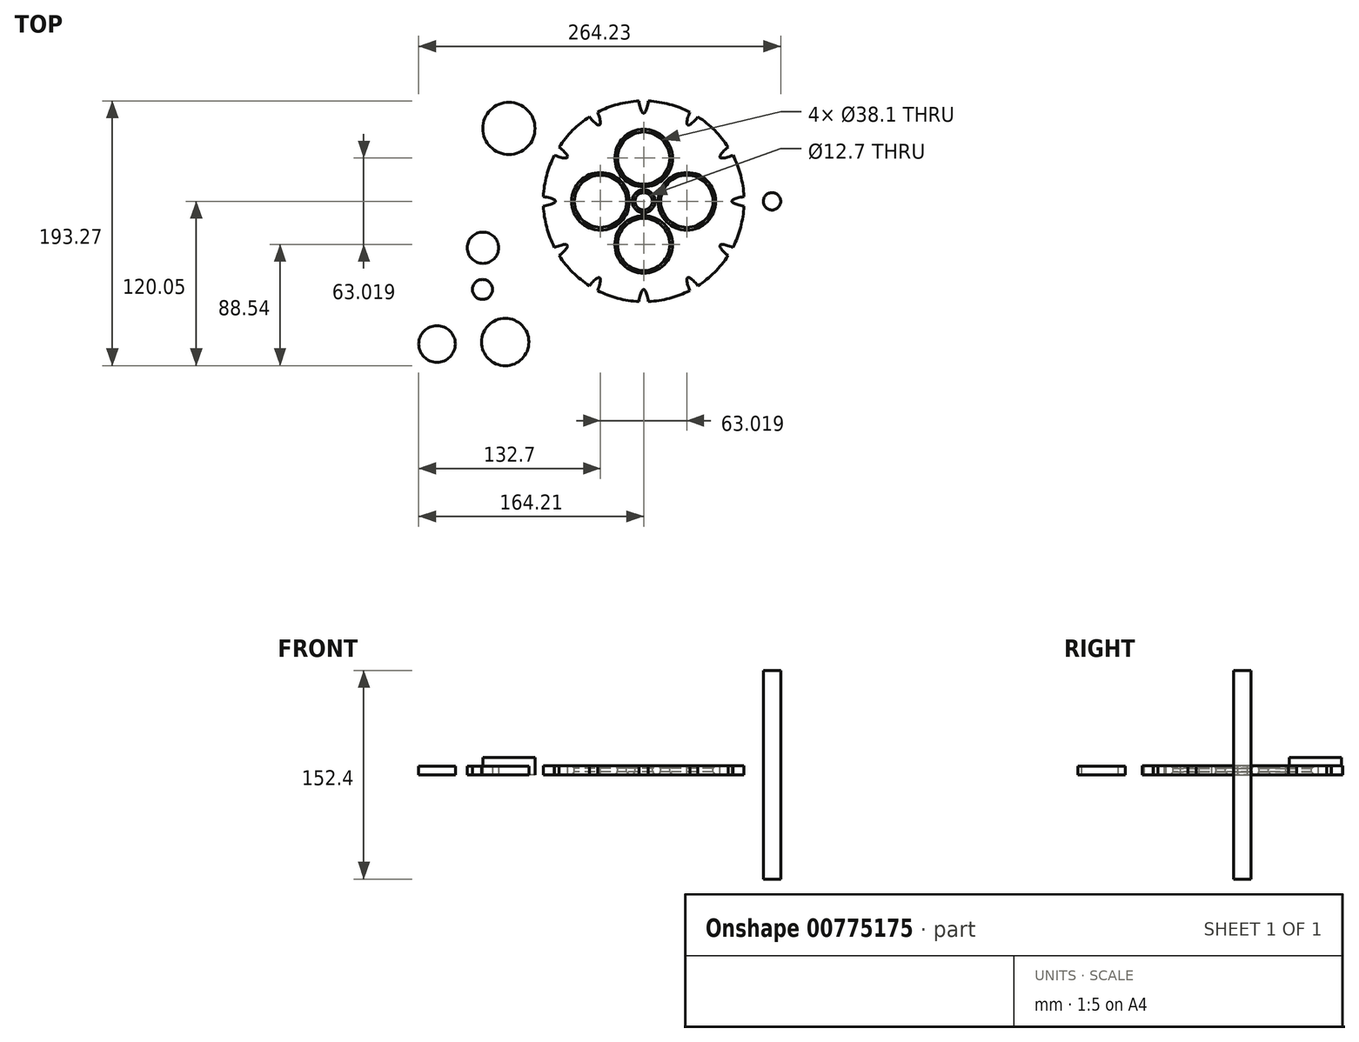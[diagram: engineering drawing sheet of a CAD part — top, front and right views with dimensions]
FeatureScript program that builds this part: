
annotation { "Feature Type Name" : "Feature", "Feature Type Description" : "" }
export const myFeature = defineFeature(function(context is Context, id is Id, definition is map)
    precondition{}
    {
        {
            var Q0;
            Q0=qCreatedBy(makeId("Top.planeOp"),FACE);
            var sketch = newSketch(context, id + "F0", { "sketchPlane" : qUnion([Q0])});
            skCircle(sketch, "E0", {"center": v(0, 0) * mm, "radius": 73.3 * mm});
            skSolve(sketch);
        }
        {
            var Q0;
            Q0=makeQuery(id+"F0.imprint","IMPRINT",FACE,{"disambiguationData":[TD([[makeQuery(id+"F0.imprint","IMPRINT",EDGE,{"derivedFrom":sQuery(id+"F0.wireOp",EDGE,"E0")}),1.0]])]});
            extrude(context, id + "F1", {"entities" : qUnion([Q0]), "depth" : 6.6 * mm, "offsetDistance" : 25.4 * mm});
        }
        {
            var Q0;
            Q0=qCreatedBy(makeId("Top.planeOp"),FACE);
            var sketch = newSketch(context, id + "F2", { "sketchPlane" : qUnion([Q0])});
            skEllipse(sketch, "E1", {"center": v(0, 87.88) * mm, "majorRadius": 23.55 * mm, "minorRadius": 4.4 * mm, "majorAxis": v(0, -1)});
            skEllipse(sketch, "E2.1.0", {"center": v(-43.94, 76.1) * mm, "majorRadius": 23.55 * mm, "minorRadius": 4.4 * mm, "majorAxis": v(0.5, -0.87)});
            skEllipse(sketch, "E2.2.0", {"center": v(-76.1, 43.94) * mm, "majorRadius": 23.55 * mm, "minorRadius": 4.4 * mm, "majorAxis": v(0.87, -0.5)});
            skEllipse(sketch, "E2.3.0", {"center": v(-87.88, 0) * mm, "majorRadius": 23.55 * mm, "minorRadius": 4.4 * mm, "majorAxis": v(1, 0)});
            skEllipse(sketch, "E2.4.0", {"center": v(-76.1, -43.94) * mm, "majorRadius": 23.55 * mm, "minorRadius": 4.4 * mm, "majorAxis": v(0.87, 0.5)});
            skEllipse(sketch, "E2.5.0", {"center": v(-43.94, -76.1) * mm, "majorRadius": 23.55 * mm, "minorRadius": 4.4 * mm, "majorAxis": v(0.5, 0.87)});
            skEllipse(sketch, "E2.6.0", {"center": v(0, -87.88) * mm, "majorRadius": 23.55 * mm, "minorRadius": 4.4 * mm, "majorAxis": v(0, 1)});
            skEllipse(sketch, "E2.7.0", {"center": v(43.94, -76.1) * mm, "majorRadius": 23.55 * mm, "minorRadius": 4.4 * mm, "majorAxis": v(-0.5, 0.87)});
            skEllipse(sketch, "E2.8.0", {"center": v(76.1, -43.94) * mm, "majorRadius": 23.55 * mm, "minorRadius": 4.4 * mm, "majorAxis": v(-0.87, 0.5)});
            skEllipse(sketch, "E2.9.0", {"center": v(87.88, 0) * mm, "majorRadius": 23.55 * mm, "minorRadius": 4.4 * mm, "majorAxis": v(-1, 0)});
            skEllipse(sketch, "E2.10.0", {"center": v(76.1, 43.94) * mm, "majorRadius": 23.55 * mm, "minorRadius": 4.4 * mm, "majorAxis": v(-0.87, -0.5)});
            skEllipse(sketch, "E2.11.0", {"center": v(43.94, 76.1) * mm, "majorRadius": 23.55 * mm, "minorRadius": 4.4 * mm, "majorAxis": v(-0.5, -0.87)});
            skPoint(sketch, "E2.center", {"position": v(0, 0) * mm});
            skSolve(sketch);
        }
        {
            var Q0;
            Q0=makeQuery(id+"F2.imprint","IMPRINT",FACE,{"disambiguationData":[TD([[makeQuery(id+"F2.imprint","IMPRINT",EDGE,{"derivedFrom":sQuery(id+"F2.wireOp",EDGE,"E1")}),1.0]])]});
            extrude(context, id + "F3", {"entities" : qUnion([Q0]), "operationType" : NewBodyOperationType.REMOVE, "depth" : 25.4 * mm, "offsetDistance" : 25.4 * mm, "hasSecondDirection" : true, "secondDirectionOppositeDirection" : true, "secondDirectionDepth" : 25.4 * mm});
        }
        {
            var Q0;
            Q0 = qSketchRegion(id + "F2", true);
            extrude(context, id + "F4", {"entities" : qUnion([Q0]), "operationType" : NewBodyOperationType.REMOVE, "depth" : 25.4 * mm, "offsetDistance" : 25.4 * mm, "hasSecondDirection" : true, "secondDirectionOppositeDirection" : true, "secondDirectionDepth" : 25.4 * mm});
        }
        {
            var Q0;
            Q0=makeQuery(id+"F1.opExtrude","CAP_FACE",FACE,{"disambiguationData":[OSD([sQuery(id+"F0.wireOp",EDGE,"E0")])],"isStart":false});
            var sketch = newSketch(context, id + "F5", { "sketchPlane" : qUnion([Q0])});
            skCircle(sketch, "E3", {"center": v(0, 31.5) * mm, "radius": 19.05 * mm});
            skCircle(sketch, "E4.1.0", {"center": v(-31.5, 0) * mm, "radius": 19.05 * mm});
            skCircle(sketch, "E4.2.0", {"center": v(0, -31.5) * mm, "radius": 19.05 * mm});
            skCircle(sketch, "E4.3.0", {"center": v(31.5, 0) * mm, "radius": 19.05 * mm});
            skPoint(sketch, "E4.center", {"position": v(0, 0) * mm});
            skSolve(sketch);
        }
        {
            var Q0;
            Q0=makeQuery(id+"F5.imprint","IMPRINT",FACE,{"disambiguationData":[TD([[makeQuery(id+"F5.imprint","IMPRINT",EDGE,{"derivedFrom":sQuery(id+"F5.wireOp",EDGE,"E3")}),1.0]])]});
            var Q1;
            Q1=makeQuery(id+"F5.imprint","IMPRINT",FACE,{"disambiguationData":[TD([[makeQuery(id+"F5.imprint","IMPRINT",EDGE,{"derivedFrom":sQuery(id+"F5.wireOp",EDGE,"E4.1.0")}),1.0]])]});
            var Q2;
            Q2=makeQuery(id+"F5.imprint","IMPRINT",FACE,{"disambiguationData":[TD([[makeQuery(id+"F5.imprint","IMPRINT",EDGE,{"derivedFrom":sQuery(id+"F5.wireOp",EDGE,"E4.3.0")}),1.0]])]});
            var Q3;
            Q3=makeQuery(id+"F5.imprint","IMPRINT",FACE,{"disambiguationData":[TD([[makeQuery(id+"F5.imprint","IMPRINT",EDGE,{"derivedFrom":sQuery(id+"F5.wireOp",EDGE,"E4.2.0")}),1.0]])]});
            extrude(context, id + "F6", {"entities" : qUnion([Q0, Q1, Q2, Q3]), "operationType" : NewBodyOperationType.REMOVE, "oppositeDirection" : true, "depth" : 25.4 * mm, "offsetDistance" : 25.4 * mm, "hasSecondDirection" : true, "secondDirectionOppositeDirection" : false, "secondDirectionDepth" : 25.4 * mm});
        }
        {
            var Q0;
            Q0=makeQuery(id+"F1.opExtrude","CAP_FACE",FACE,{"disambiguationData":[OSD([sQuery(id+"F0.wireOp",EDGE,"E0")])],"isStart":false});
            var sketch = newSketch(context, id + "F7", { "sketchPlane" : qUnion([Q0])});
            skCircle(sketch, "E5", {"center": v(0, 0) * mm, "radius": 6.35 * mm});
            skSolve(sketch);
        }
        {
            var Q0;
            Q0=makeQuery(id+"F7.imprint","IMPRINT",FACE,{"disambiguationData":[TD([[makeQuery(id+"F7.imprint","IMPRINT",EDGE,{"derivedFrom":sQuery(id+"F7.wireOp",EDGE,"E5")}),1.0]])]});
            extrude(context, id + "F8", {"entities" : qUnion([Q0]), "operationType" : NewBodyOperationType.REMOVE, "oppositeDirection" : true, "depth" : 25.4 * mm, "offsetDistance" : 25.4 * mm, "hasSecondDirection" : true, "secondDirectionOppositeDirection" : false, "secondDirectionDepth" : 25.4 * mm});
        }
        {
            var Q0;
            Q0=makeQuery(id+"F8.boolean.opBoolean","INTERSECT",EDGE,{"derivedFrom":[makeQuery(id+"F1.opExtrude","CAP_FACE",FACE,{"disambiguationData":[OSD([sQuery(id+"F0.wireOp",EDGE,"E0")])],"isStart":false}),makeQuery(id+"F8.opExtrude","SWEPT_FACE",FACE,{"disambiguationData":[OSD([sQuery(id+"F7.wireOp",EDGE,"E5")])]})]});
            var Q1;
            Q1=makeQuery(id+"F6.boolean.opBoolean","INTERSECT",EDGE,{"derivedFrom":[makeQuery(id+"F1.opExtrude","CAP_FACE",FACE,{"disambiguationData":[OSD([sQuery(id+"F0.wireOp",EDGE,"E0")])],"isStart":false}),makeQuery(id+"F6.opExtrude","SWEPT_FACE",FACE,{"disambiguationData":[OSD([sQuery(id+"F5.wireOp",EDGE,"E4.3.0")])]})]});
            var Q2;
            Q2=makeQuery(id+"F6.boolean.opBoolean","INTERSECT",EDGE,{"derivedFrom":[makeQuery(id+"F1.opExtrude","CAP_FACE",FACE,{"disambiguationData":[OSD([sQuery(id+"F0.wireOp",EDGE,"E0")])],"isStart":false}),makeQuery(id+"F6.opExtrude","SWEPT_FACE",FACE,{"disambiguationData":[OSD([sQuery(id+"F5.wireOp",EDGE,"E4.2.0")])]})]});
            var Q3;
            Q3=makeQuery(id+"F6.boolean.opBoolean","INTERSECT",EDGE,{"derivedFrom":[makeQuery(id+"F1.opExtrude","CAP_FACE",FACE,{"disambiguationData":[OSD([sQuery(id+"F0.wireOp",EDGE,"E0")])],"isStart":false}),makeQuery(id+"F6.opExtrude","SWEPT_FACE",FACE,{"disambiguationData":[OSD([sQuery(id+"F5.wireOp",EDGE,"E4.1.0")])]})]});
            var Q4;
            Q4=makeQuery(id+"F6.boolean.opBoolean","INTERSECT",EDGE,{"derivedFrom":[makeQuery(id+"F1.opExtrude","CAP_FACE",FACE,{"disambiguationData":[OSD([sQuery(id+"F0.wireOp",EDGE,"E0")])],"isStart":false}),makeQuery(id+"F6.opExtrude","SWEPT_FACE",FACE,{"disambiguationData":[OSD([sQuery(id+"F5.wireOp",EDGE,"E3")])]})]});
            var Q5;
            Q5=makeQuery(id+"F8.boolean.opBoolean","INTERSECT",EDGE,{"derivedFrom":[makeQuery(id+"F1.opExtrude","CAP_FACE",FACE,{"disambiguationData":[OSD([sQuery(id+"F0.wireOp",EDGE,"E0")])],"isStart":true}),makeQuery(id+"F8.opExtrude","SWEPT_FACE",FACE,{"disambiguationData":[OSD([sQuery(id+"F7.wireOp",EDGE,"E5")])]})]});
            var Q6;
            Q6=makeQuery(id+"F6.boolean.opBoolean","INTERSECT",EDGE,{"derivedFrom":[makeQuery(id+"F1.opExtrude","CAP_FACE",FACE,{"disambiguationData":[OSD([sQuery(id+"F0.wireOp",EDGE,"E0")])],"isStart":true}),makeQuery(id+"F6.opExtrude","SWEPT_FACE",FACE,{"disambiguationData":[OSD([sQuery(id+"F5.wireOp",EDGE,"E3")])]})]});
            var Q7;
            Q7=makeQuery(id+"F6.boolean.opBoolean","INTERSECT",EDGE,{"derivedFrom":[makeQuery(id+"F1.opExtrude","CAP_FACE",FACE,{"disambiguationData":[OSD([sQuery(id+"F0.wireOp",EDGE,"E0")])],"isStart":true}),makeQuery(id+"F6.opExtrude","SWEPT_FACE",FACE,{"disambiguationData":[OSD([sQuery(id+"F5.wireOp",EDGE,"E4.3.0")])]})]});
            var Q8;
            Q8=makeQuery(id+"F6.boolean.opBoolean","INTERSECT",EDGE,{"derivedFrom":[makeQuery(id+"F1.opExtrude","CAP_FACE",FACE,{"disambiguationData":[OSD([sQuery(id+"F0.wireOp",EDGE,"E0")])],"isStart":true}),makeQuery(id+"F6.opExtrude","SWEPT_FACE",FACE,{"disambiguationData":[OSD([sQuery(id+"F5.wireOp",EDGE,"E4.2.0")])]})]});
            var Q9;
            Q9=makeQuery(id+"F6.boolean.opBoolean","INTERSECT",EDGE,{"derivedFrom":[makeQuery(id+"F1.opExtrude","CAP_FACE",FACE,{"disambiguationData":[OSD([sQuery(id+"F0.wireOp",EDGE,"E0")])],"isStart":true}),makeQuery(id+"F6.opExtrude","SWEPT_FACE",FACE,{"disambiguationData":[OSD([sQuery(id+"F5.wireOp",EDGE,"E4.1.0")])]})]});
            chamfer(context, id + "F9", {"entities" : qUnion([Q0, Q1, Q2, Q3, Q4, Q5, Q6, Q7, Q8, Q9]), "width" : 2.03 * mm, "tangentPropagation" : true});
        }
        {
            var Q0;
            Q0=qCreatedBy(makeId("Top.planeOp"),FACE);
            var sketch = newSketch(context, id + "F10", { "sketchPlane" : qUnion([Q0])});
            skCircle(sketch, "E6", {"center": v(93.67, 0) * mm, "radius": 6.35 * mm});
            skSolve(sketch);
        }
        {
            var Q0;
            Q0=makeQuery(id+"F10.imprint","IMPRINT",FACE,{"disambiguationData":[TD([[makeQuery(id+"F10.imprint","IMPRINT",EDGE,{"derivedFrom":sQuery(id+"F10.wireOp",EDGE,"E6")}),1.0]])]});
            extrude(context, id + "F11", {"entities" : qUnion([Q0]), "endBound" : BoundingType.SYMMETRIC, "oppositeDirection" : true, "depth" : 152.4 * mm, "offsetDistance" : 25.4 * mm});
        }
        {
            var Q0;
            Q0=qCreatedBy(makeId("Top.planeOp"),FACE);
            var sketch = newSketch(context, id + "F12", { "sketchPlane" : qUnion([Q0])});
            skCircle(sketch, "E7", {"center": v(-98.36, 53.22) * mm, "radius": 19.05 * mm});
            skSolve(sketch);
        }
        {
            var Q0;
            Q0=makeQuery(id+"F12.imprint","IMPRINT",FACE,{"disambiguationData":[TD([[makeQuery(id+"F12.imprint","IMPRINT",EDGE,{"derivedFrom":sQuery(id+"F12.wireOp",EDGE,"E7")}),1.0]])]});
            extrude(context, id + "F13", {"entities" : qUnion([Q0]), "depth" : 12.7 * mm, "offsetDistance" : 25.4 * mm});
        }
        {
            var Q0;
            Q0=qCreatedBy(makeId("Top.planeOp"),FACE);
            var sketch = newSketch(context, id + "F14", { "sketchPlane" : qUnion([Q0])});
            skCircle(sketch, "E8", {"center": v(-101.03, -102.78) * mm, "radius": 17.27 * mm});
            skCircle(sketch, "E9", {"center": v(-117.65, -64.37) * mm, "radius": 7.3 * mm});
            skCircle(sketch, "E10", {"center": v(-117.31, -33.93) * mm, "radius": 11.45 * mm});
            skCircle(sketch, "E11", {"center": v(-150.85, -104.22) * mm, "radius": 13.36 * mm});
            skSolve(sketch);
        }
        {
            var Q0;
            Q0 = qSketchRegion(id + "F14", true);
            extrude(context, id + "F15", {"entities" : qUnion([Q0]), "depth" : 6.35 * mm, "offsetDistance" : 25.4 * mm});
        }
    });
